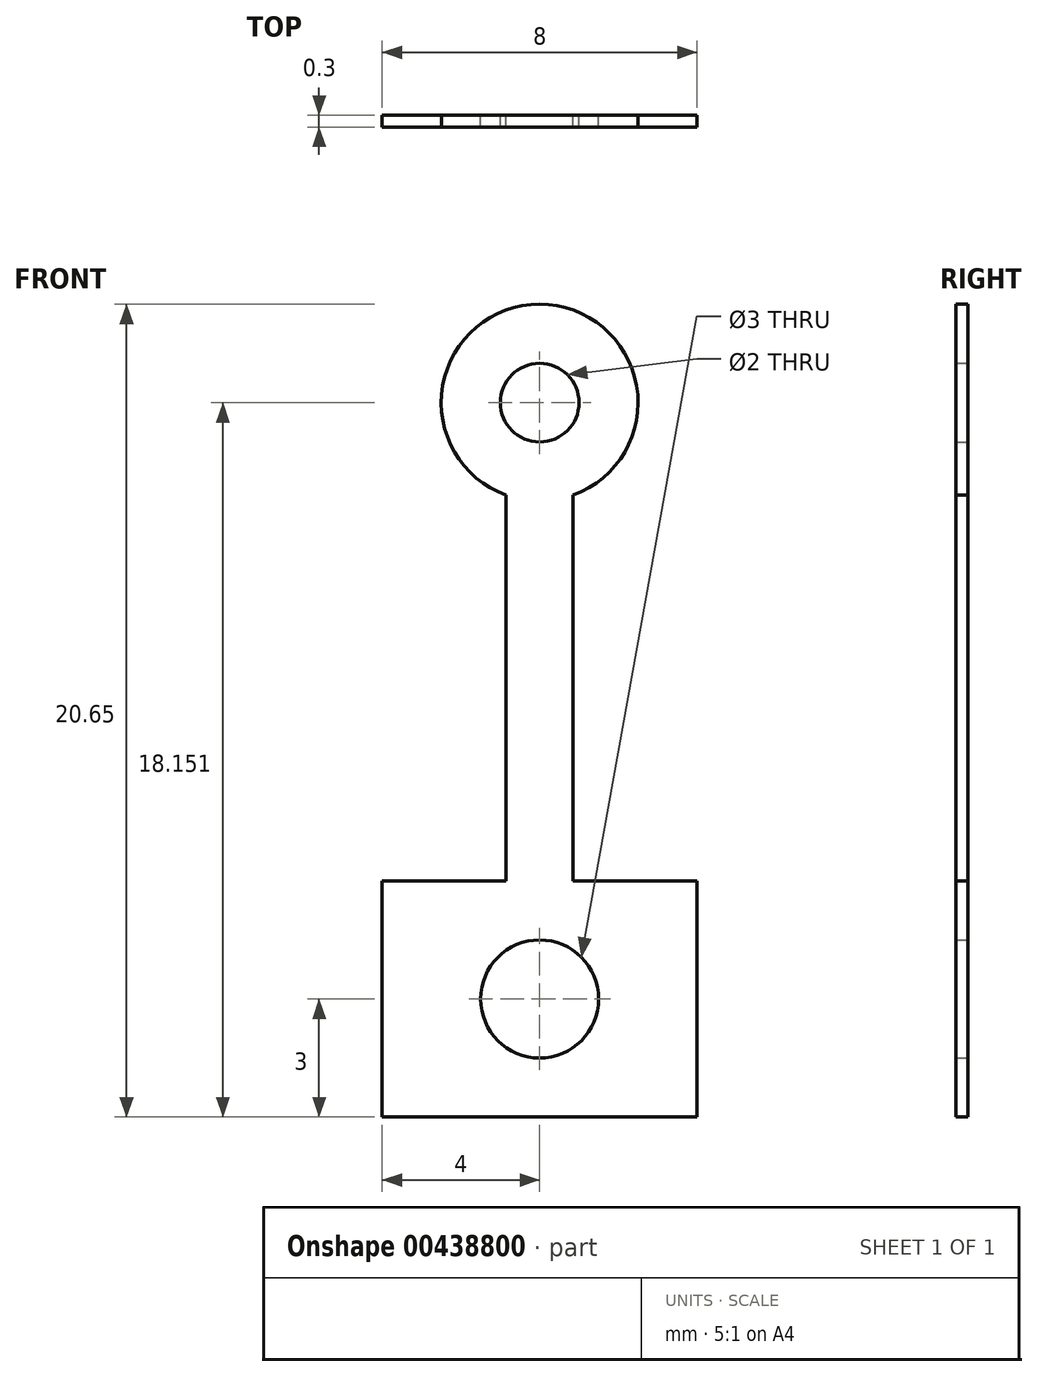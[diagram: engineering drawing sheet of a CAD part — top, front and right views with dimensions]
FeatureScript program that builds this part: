
annotation { "Feature Type Name" : "Feature", "Feature Type Description" : "" }
export const myFeature = defineFeature(function(context is Context, id is Id, definition is map)
    precondition{}
    {
        {
            var Q0;
            Q0=qCreatedBy(makeId("Front.planeOp"),FACE);
            var sketch = newSketch(context, id + "F0", { "sketchPlane" : qUnion([Q0])});
            skLineSegment(sketch, "E0.bottom", {"start": v(4, -3) * mm, "end": v(-4, -3) * mm});
            skLineSegment(sketch, "E0.top", {"start": v(4, 3) * mm, "end": v(0.85, 3) * mm});
            skLineSegment(sketch, "E0.left", {"start": v(4, -3) * mm, "end": v(4, 3) * mm});
            skLineSegment(sketch, "E0.right", {"start": v(-4, -3) * mm, "end": v(-4, 3) * mm});
            skPoint(sketch, "E0.middle", {"position": v(0, 0) * mm});
            skCircle(sketch, "E1", {"center": v(0, 0) * mm, "radius": 1.5 * mm});
            skLineSegment(sketch, "E2", {"start": v(-0.85, 12.8) * mm, "end": v(-0.85, 3) * mm});
            skLineSegment(sketch, "E3.MirrorCS", {"start": v(0.85, 12.8) * mm, "end": v(0.85, 3) * mm});
            skArc(sketch, "E4", {"start": v(0.85, 12.8) * mm, "mid": v(0, 17.65) * mm, "end": v(-0.85, 12.8) * mm});
            skCircle(sketch, "E5", {"center": v(0, 15.15) * mm, "radius": 1 * mm});
            skLineSegment(sketch, "E6.trimOffspring", {"start": v(-0.85, 3) * mm, "end": v(-4, 3) * mm});
            skSolve(sketch);
        }
        {
            var Q0;
            Q0=makeQuery(id+"F0.imprint","IMPRINT",FACE,{"disambiguationData":[TD([[makeQuery(id+"F0.imprint","IMPRINT",EDGE,{"derivedFrom":sQuery(id+"F0.wireOp",EDGE,"E0.bottom")}),-1.0]])]});
            extrude(context, id + "F1", {"entities" : qUnion([Q0]), "depth" : .3 * mm});
        }
    });
